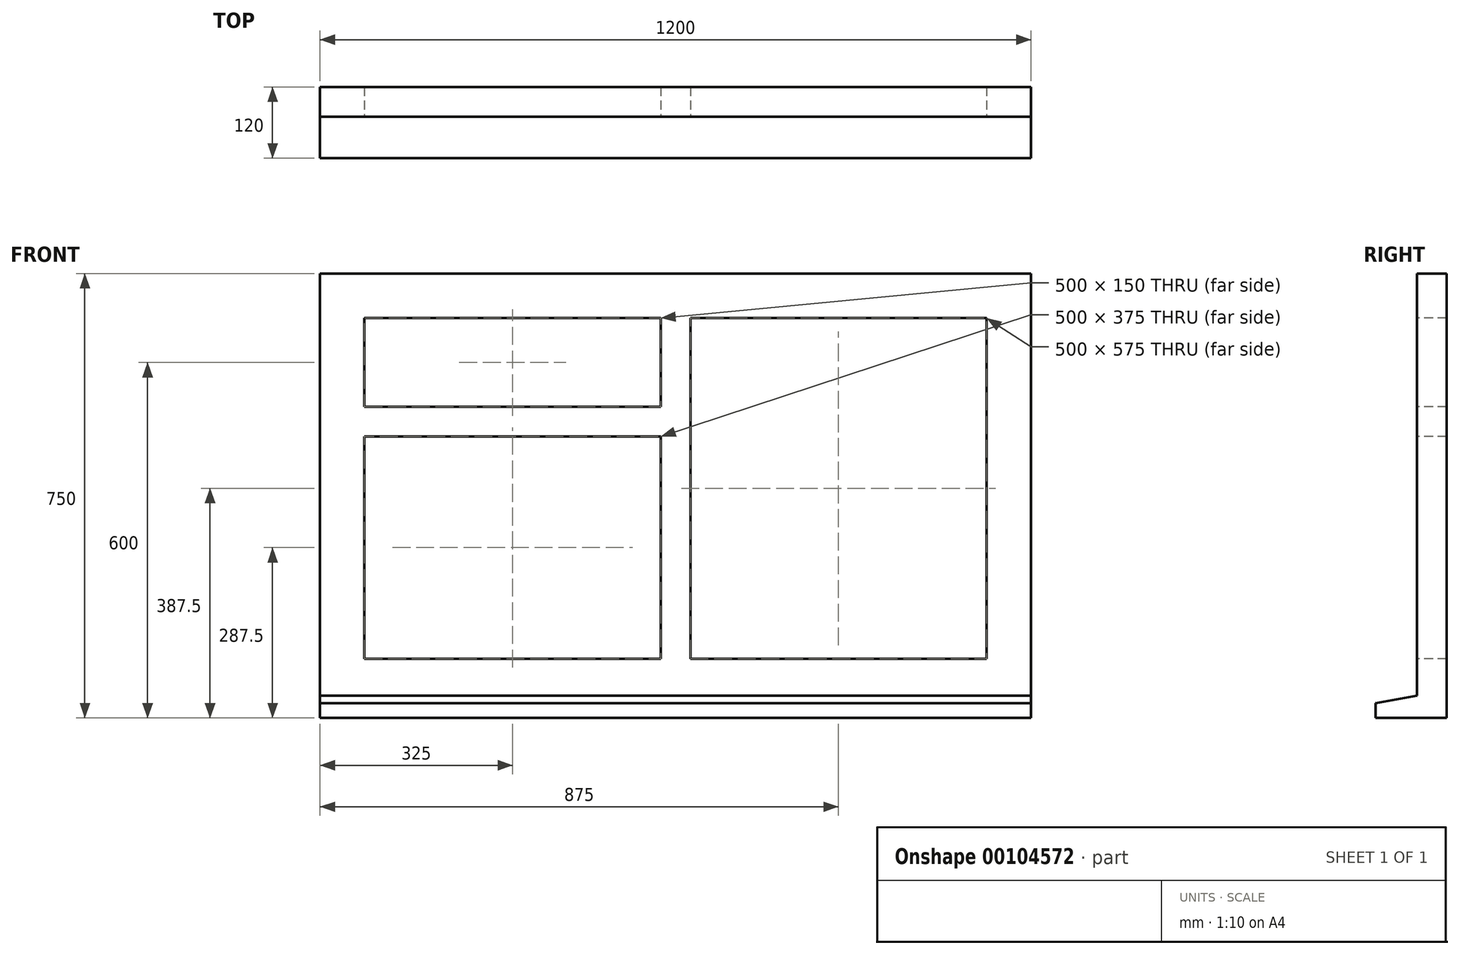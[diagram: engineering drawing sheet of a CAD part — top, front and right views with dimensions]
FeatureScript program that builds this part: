
annotation { "Feature Type Name" : "Feature", "Feature Type Description" : "" }
export const myFeature = defineFeature(function(context is Context, id is Id, definition is map)
    precondition{}
    {
        {
            var Q0;
            Q0=qCreatedBy(makeId("Front.planeOp"),FACE);
            var sketch = newSketch(context, id + "F0", { "sketchPlane" : qUnion([Q0])});
            skLineSegment(sketch, "E0.bottom", {"start": v(0, 0) * mm, "end": v(1200, 0) * mm});
            skLineSegment(sketch, "E0.top", {"start": v(0, -750) * mm, "end": v(1200, -750) * mm});
            skLineSegment(sketch, "E0.left", {"start": v(0, 0) * mm, "end": v(0, -750) * mm});
            skLineSegment(sketch, "E0.right", {"start": v(1200, 0) * mm, "end": v(1200, -750) * mm});
            skLineSegment(sketch, "E1.bottom", {"start": v(625, -75) * mm, "end": v(1125, -75) * mm});
            skLineSegment(sketch, "E1.top", {"start": v(625, -650) * mm, "end": v(1125, -650) * mm});
            skLineSegment(sketch, "E1.left", {"start": v(625, -75) * mm, "end": v(625, -650) * mm});
            skLineSegment(sketch, "E1.right", {"start": v(1125, -75) * mm, "end": v(1125, -650) * mm});
            skLineSegment(sketch, "E2.bottom", {"start": v(75, -275) * mm, "end": v(575, -275) * mm});
            skLineSegment(sketch, "E2.top", {"start": v(75, -650) * mm, "end": v(575, -650) * mm});
            skLineSegment(sketch, "E2.left", {"start": v(75, -275) * mm, "end": v(75, -650) * mm});
            skLineSegment(sketch, "E2.right", {"start": v(575, -275) * mm, "end": v(575, -650) * mm});
            skLineSegment(sketch, "E3.bottom", {"start": v(75, -75) * mm, "end": v(575, -75) * mm});
            skLineSegment(sketch, "E3.top", {"start": v(75, -225) * mm, "end": v(575, -225) * mm});
            skLineSegment(sketch, "E3.left", {"start": v(75, -75) * mm, "end": v(75, -225) * mm});
            skLineSegment(sketch, "E3.right", {"start": v(575, -75) * mm, "end": v(575, -225) * mm});
            skPoint(sketch, "E4.firstSnap0", {"position": v(325, -225) * mm});
            skSolve(sketch);
        }
        {
            var Q0;
            Q0 = qSketchRegion(id + "F0", true);
            extrude(context, id + "F1", {"entities" : qUnion([Q0]), "oppositeDirection" : true, "depth" : 50 * mm});
        }
        {
            var Q0;
            Q0=makeQuery(id+"F1.opExtrude","SWEPT_FACE",FACE,{"disambiguationData":[OSD([sQuery(id+"F0.wireOp",EDGE,"E0.right")])]});
            var sketch = newSketch(context, id + "F2", { "sketchPlane" : qUnion([Q0])});
            skLineSegment(sketch, "E5", {"start": v(0, -750) * mm, "end": v(-70, -750) * mm});
            skLineSegment(sketch, "E6", {"start": v(0, -712.66) * mm, "end": v(-70, -725) * mm});
            skLineSegment(sketch, "E7", {"start": v(-70, -725) * mm, "end": v(-70, -750) * mm});
            skLineSegment(sketch, "E8", {"start": v(0, -750) * mm, "end": v(0, -712.66) * mm});
            skSolve(sketch);
        }
        {
            var Q0;
            Q0 = qSketchRegion(id + "F2", true);
            extrude(context, id + "F3", {"entities" : qUnion([Q0]), "operationType" : NewBodyOperationType.ADD, "oppositeDirection" : true, "depth" : 1200 * mm});
        }
    });
